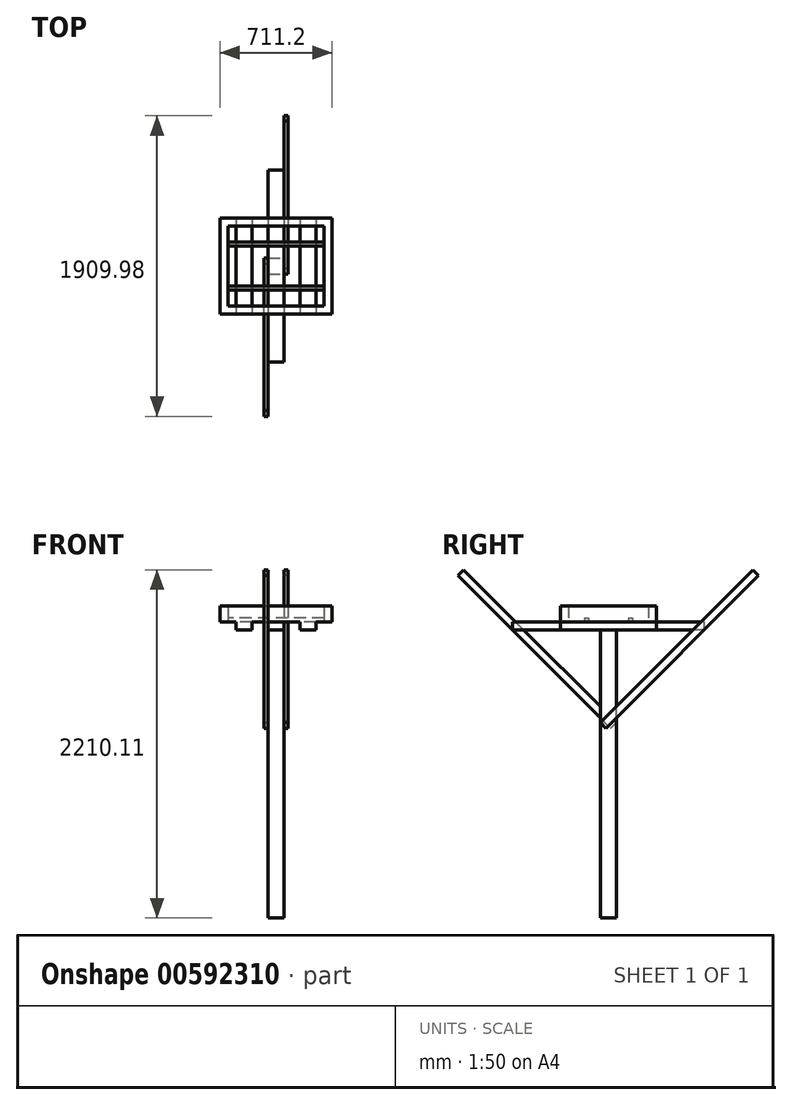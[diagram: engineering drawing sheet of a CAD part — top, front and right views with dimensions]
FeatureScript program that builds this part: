
annotation { "Feature Type Name" : "Feature", "Feature Type Description" : "" }
export const myFeature = defineFeature(function(context is Context, id is Id, definition is map)
    precondition{}
    {
        {
            var Q0;
            Q0=qCreatedBy(makeId("Top.planeOp"),FACE);
            var sketch = newSketch(context, id + "F0", { "sketchPlane" : qUnion([Q0])});
            skLineSegment(sketch, "E0.bottom", {"start": v(0, 0) * mm, "end": v(50.8, 0) * mm});
            skLineSegment(sketch, "E0.top", {"start": v(0, -609.6) * mm, "end": v(50.8, -609.6) * mm});
            skLineSegment(sketch, "E0.left", {"start": v(0, 0) * mm, "end": v(0, -609.6) * mm});
            skLineSegment(sketch, "E0.right", {"start": v(50.8, 0) * mm, "end": v(50.8, -609.6) * mm});
            skLineSegment(sketch, "E1.bottom", {"start": v(50.8, -609.6) * mm, "end": v(660.4, -609.6) * mm});
            skLineSegment(sketch, "E1.top", {"start": v(50.8, -558.8) * mm, "end": v(660.4, -558.8) * mm});
            skLineSegment(sketch, "E1.left", {"start": v(50.8, -609.6) * mm, "end": v(50.8, -558.8) * mm});
            skLineSegment(sketch, "E1.right", {"start": v(660.4, -609.6) * mm, "end": v(660.4, -558.8) * mm});
            skLineSegment(sketch, "E2.bottom", {"start": v(660.4, -609.6) * mm, "end": v(711.2, -609.6) * mm});
            skLineSegment(sketch, "E2.top", {"start": v(660.4, 0) * mm, "end": v(711.2, 0) * mm});
            skLineSegment(sketch, "E2.left", {"start": v(660.4, -609.6) * mm, "end": v(660.4, 0) * mm});
            skLineSegment(sketch, "E2.right", {"start": v(711.2, -609.6) * mm, "end": v(711.2, 0) * mm});
            skLineSegment(sketch, "E3.bottom", {"start": v(660.4, 0) * mm, "end": v(50.8, 0) * mm});
            skLineSegment(sketch, "E3.top", {"start": v(660.4, -50.8) * mm, "end": v(50.8, -50.8) * mm});
            skLineSegment(sketch, "E3.left", {"start": v(660.4, 0) * mm, "end": v(660.4, -50.8) * mm});
            skLineSegment(sketch, "E3.right", {"start": v(50.8, 0) * mm, "end": v(50.8, -50.8) * mm});
            skSolve(sketch);
        }
        {
            var Q0;
            Q0 = qSketchRegion(id + "F0", true);
            extrude(context, id + "F1", {"entities" : qUnion([Q0]), "oppositeDirection" : true, "depth" : 101.6 * mm, "offsetDistance" : 25.4 * mm});
        }
        {
            var Q0;
            Q0=qCreatedBy(makeId("Top.planeOp"),FACE);
            var sketch = newSketch(context, id + "F2", { "sketchPlane" : qUnion([Q0])});
            skLineSegment(sketch, "E4.bottom", {"start": v(101.6, 0) * mm, "end": v(203.2, 0) * mm});
            skLineSegment(sketch, "E4.top", {"start": v(101.6, -609.6) * mm, "end": v(203.2, -609.6) * mm});
            skLineSegment(sketch, "E4.left", {"start": v(101.6, 0) * mm, "end": v(101.6, -609.6) * mm});
            skLineSegment(sketch, "E4.right", {"start": v(203.2, 0) * mm, "end": v(203.2, -609.6) * mm});
            skLineSegment(sketch, "E5.bottom", {"start": v(508, 0) * mm, "end": v(609.6, 0) * mm});
            skLineSegment(sketch, "E5.top", {"start": v(508, -609.6) * mm, "end": v(609.6, -609.6) * mm});
            skLineSegment(sketch, "E5.left", {"start": v(508, 0) * mm, "end": v(508, -609.6) * mm});
            skLineSegment(sketch, "E5.right", {"start": v(609.6, 0) * mm, "end": v(609.6, -609.6) * mm});
            skLineSegment(sketch, "E6.bottom", {"start": v(304.8, 304.8) * mm, "end": v(406.4, 304.8) * mm});
            skLineSegment(sketch, "E6.top", {"start": v(304.8, -914.4) * mm, "end": v(406.4, -914.4) * mm});
            skLineSegment(sketch, "E6.left", {"start": v(304.8, 304.8) * mm, "end": v(304.8, -914.4) * mm});
            skLineSegment(sketch, "E6.right", {"start": v(406.4, 304.8) * mm, "end": v(406.4, -914.4) * mm});
            skSolve(sketch);
        }
        {
            var Q0;
            Q0 = qSketchRegion(id + "F2", true);
            extrude(context, id + "F3", {"entities" : qUnion([Q0]), "operationType" : NewBodyOperationType.ADD, "depth" : 50.8 * mm, "offsetDistance" : 25.4 * mm});
        }
        {
            var Q0;
            Q0=makeQuery(id+"F3.opExtrude","CAP_FACE",FACE,{"disambiguationData":[OSD([sQuery(id+"F2.wireOp",EDGE,"E6.bottom"),sQuery(id+"F2.wireOp",EDGE,"E6.top"),sQuery(id+"F2.wireOp",EDGE,"E6.left"),sQuery(id+"F2.wireOp",EDGE,"E6.right")])],"isStart":false});
            var sketch = newSketch(context, id + "F4", { "sketchPlane" : qUnion([Q0])});
            skLineSegment(sketch, "E7.bottom", {"start": v(304.8, -254) * mm, "end": v(406.4, -254) * mm});
            skLineSegment(sketch, "E7.top", {"start": v(304.8, -355.6) * mm, "end": v(406.4, -355.6) * mm});
            skLineSegment(sketch, "E7.left", {"start": v(304.8, -254) * mm, "end": v(304.8, -355.6) * mm});
            skLineSegment(sketch, "E7.right", {"start": v(406.4, -254) * mm, "end": v(406.4, -355.6) * mm});
            skSolve(sketch);
        }
        {
            var Q0;
            Q0 = qSketchRegion(id + "F4", true);
            extrude(context, id + "F5", {"entities" : qUnion([Q0]), "operationType" : NewBodyOperationType.ADD, "depth" : 1828.8 * mm, "offsetDistance" : 25.4 * mm});
        }
        {
            var Q0;
            Q0=makeQuery(id+"F5.boolean.opBoolean","MERGE",FACE,{"derivedFrom":[makeQuery(id+"F3.opExtrude","SWEPT_FACE",FACE,{"disambiguationData":[OSD([sQuery(id+"F2.wireOp",EDGE,"E6.right")])]}),makeQuery(id+"F5.opExtrude","SWEPT_FACE",FACE,{"disambiguationData":[OSD([sQuery(id+"F4.wireOp",EDGE,"E7.right")])]})]});
            var sketch = newSketch(context, id + "F6", { "sketchPlane" : qUnion([Q0])});
            skLineSegment(sketch, "E8.bottom", {"start": v(650.19, -294.59) * mm, "end": v(614.27, -330.5) * mm});
            skLineSegment(sketch, "E8.top", {"start": v(-319.68, 675.28) * mm, "end": v(-355.6, 639.36) * mm});
            skLineSegment(sketch, "E8.left", {"start": v(650.19, -294.59) * mm, "end": v(-319.68, 675.28) * mm});
            skLineSegment(sketch, "E8.right", {"start": v(614.27, -330.5) * mm, "end": v(-355.6, 639.36) * mm});
            skSolve(sketch);
        }
        {
            var Q0;
            Q0 = qSketchRegion(id + "F6", true);
            extrude(context, id + "F7", {"entities" : qUnion([Q0]), "operationType" : NewBodyOperationType.ADD, "depth" : 25.4 * mm, "offsetDistance" : 25.4 * mm});
        }
        {
            var Q0;
            Q0=makeQuery(id+"F5.boolean.opBoolean","MERGE",FACE,{"derivedFrom":[makeQuery(id+"F3.opExtrude","SWEPT_FACE",FACE,{"disambiguationData":[OSD([sQuery(id+"F2.wireOp",EDGE,"E6.left")])]}),makeQuery(id+"F5.opExtrude","SWEPT_FACE",FACE,{"disambiguationData":[OSD([sQuery(id+"F4.wireOp",EDGE,"E7.left")])]})]});
            var sketch = newSketch(context, id + "F8", { "sketchPlane" : qUnion([Q0])});
            skLineSegment(sketch, "E9.bottom", {"start": v(1259.79, -294.59) * mm, "end": v(1223.87, -330.5) * mm});
            skLineSegment(sketch, "E9.top", {"start": v(289.92, 675.28) * mm, "end": v(254, 639.36) * mm});
            skLineSegment(sketch, "E9.left", {"start": v(1259.79, -294.59) * mm, "end": v(289.92, 675.28) * mm});
            skLineSegment(sketch, "E9.right", {"start": v(1223.87, -330.5) * mm, "end": v(254, 639.36) * mm});
            skSolve(sketch);
        }
        {
            var Q0;
            Q0 = qSketchRegion(id + "F8", true);
            extrude(context, id + "F9", {"entities" : qUnion([Q0]), "operationType" : NewBodyOperationType.ADD, "depth" : 25.4 * mm, "offsetDistance" : 25.4 * mm});
        }
        {
            var Q0;
            Q0=makeQuery(id+"F3.opExtrude","CAP_FACE",FACE,{"disambiguationData":[OSD([sQuery(id+"F2.wireOp",EDGE,"E5.bottom"),sQuery(id+"F2.wireOp",EDGE,"E5.top"),sQuery(id+"F2.wireOp",EDGE,"E5.left"),sQuery(id+"F2.wireOp",EDGE,"E5.right")])],"isStart":true});
            var sketch = newSketch(context, id + "F10", { "sketchPlane" : qUnion([Q0])});
            skLineSegment(sketch, "E10.bottom", {"start": v(660.4, 457.2) * mm, "end": v(50.8, 457.2) * mm});
            skLineSegment(sketch, "E10.top", {"start": v(660.4, 431.8) * mm, "end": v(50.8, 431.8) * mm});
            skLineSegment(sketch, "E10.left", {"start": v(660.4, 457.2) * mm, "end": v(660.4, 431.8) * mm});
            skLineSegment(sketch, "E10.right", {"start": v(50.8, 457.2) * mm, "end": v(50.8, 431.8) * mm});
            skLineSegment(sketch, "E11.bottom", {"start": v(660.4, 177.8) * mm, "end": v(50.8, 177.8) * mm});
            skLineSegment(sketch, "E11.top", {"start": v(660.4, 152.4) * mm, "end": v(50.8, 152.4) * mm});
            skLineSegment(sketch, "E11.left", {"start": v(660.4, 177.8) * mm, "end": v(660.4, 152.4) * mm});
            skLineSegment(sketch, "E11.right", {"start": v(50.8, 177.8) * mm, "end": v(50.8, 152.4) * mm});
            skSolve(sketch);
        }
        {
            var Q0;
            Q0 = qSketchRegion(id + "F10", true);
            extrude(context, id + "F11", {"entities" : qUnion([Q0]), "operationType" : NewBodyOperationType.ADD, "depth" : 25.4 * mm, "offsetDistance" : 25.4 * mm});
        }
        {
            var Q0;
            Q0=makeQuery(id+"F1.opExtrude","SWEPT_BODY",BODY,{"disambiguationData":[OSD([sQuery(id+"F0.wireOp",EDGE,"E0.bottom"),sQuery(id+"F0.wireOp",EDGE,"E0.top"),sQuery(id+"F0.wireOp",EDGE,"E0.left"),sQuery(id+"F0.wireOp",EDGE,"E0.right"),sQuery(id+"F0.wireOp",EDGE,"E1.bottom"),sQuery(id+"F0.wireOp",EDGE,"E1.top"),sQuery(id+"F0.wireOp",EDGE,"E2.bottom"),sQuery(id+"F0.wireOp",EDGE,"E2.top"),sQuery(id+"F0.wireOp",EDGE,"E2.left"),sQuery(id+"F0.wireOp",EDGE,"E2.right"),sQuery(id+"F0.wireOp",EDGE,"E3.bottom"),sQuery(id+"F0.wireOp",EDGE,"E3.top")])]});
            var Q1;
            Q1=makeQuery(id+"F1.opExtrude","CAP_FACE",FACE,{"disambiguationData":[OSD([sQuery(id+"F0.wireOp",EDGE,"E0.bottom"),sQuery(id+"F0.wireOp",EDGE,"E0.top"),sQuery(id+"F0.wireOp",EDGE,"E0.left"),sQuery(id+"F0.wireOp",EDGE,"E0.right"),sQuery(id+"F0.wireOp",EDGE,"E1.bottom"),sQuery(id+"F0.wireOp",EDGE,"E1.top"),sQuery(id+"F0.wireOp",EDGE,"E2.bottom"),sQuery(id+"F0.wireOp",EDGE,"E2.top"),sQuery(id+"F0.wireOp",EDGE,"E2.left"),sQuery(id+"F0.wireOp",EDGE,"E2.right"),sQuery(id+"F0.wireOp",EDGE,"E3.bottom"),sQuery(id+"F0.wireOp",EDGE,"E3.top")])],"isStart":false});
            mirror(context, id + "F12", {"entities" : qUnion([Q0]), "mirrorPlane" : qUnion([Q1])});
        }
        {
            var Q0;
            Q0=makeQuery(id+"F1.opExtrude","SWEPT_BODY",BODY,{"disambiguationData":[OSD([sQuery(id+"F0.wireOp",EDGE,"E0.bottom"),sQuery(id+"F0.wireOp",EDGE,"E0.top"),sQuery(id+"F0.wireOp",EDGE,"E0.left"),sQuery(id+"F0.wireOp",EDGE,"E0.right"),sQuery(id+"F0.wireOp",EDGE,"E1.bottom"),sQuery(id+"F0.wireOp",EDGE,"E1.top"),sQuery(id+"F0.wireOp",EDGE,"E2.bottom"),sQuery(id+"F0.wireOp",EDGE,"E2.top"),sQuery(id+"F0.wireOp",EDGE,"E2.left"),sQuery(id+"F0.wireOp",EDGE,"E2.right"),sQuery(id+"F0.wireOp",EDGE,"E3.bottom"),sQuery(id+"F0.wireOp",EDGE,"E3.top")])]});
            deleteBodies(context, id + "F13", {"entities" : qUnion([Q0])});
        }
    });
